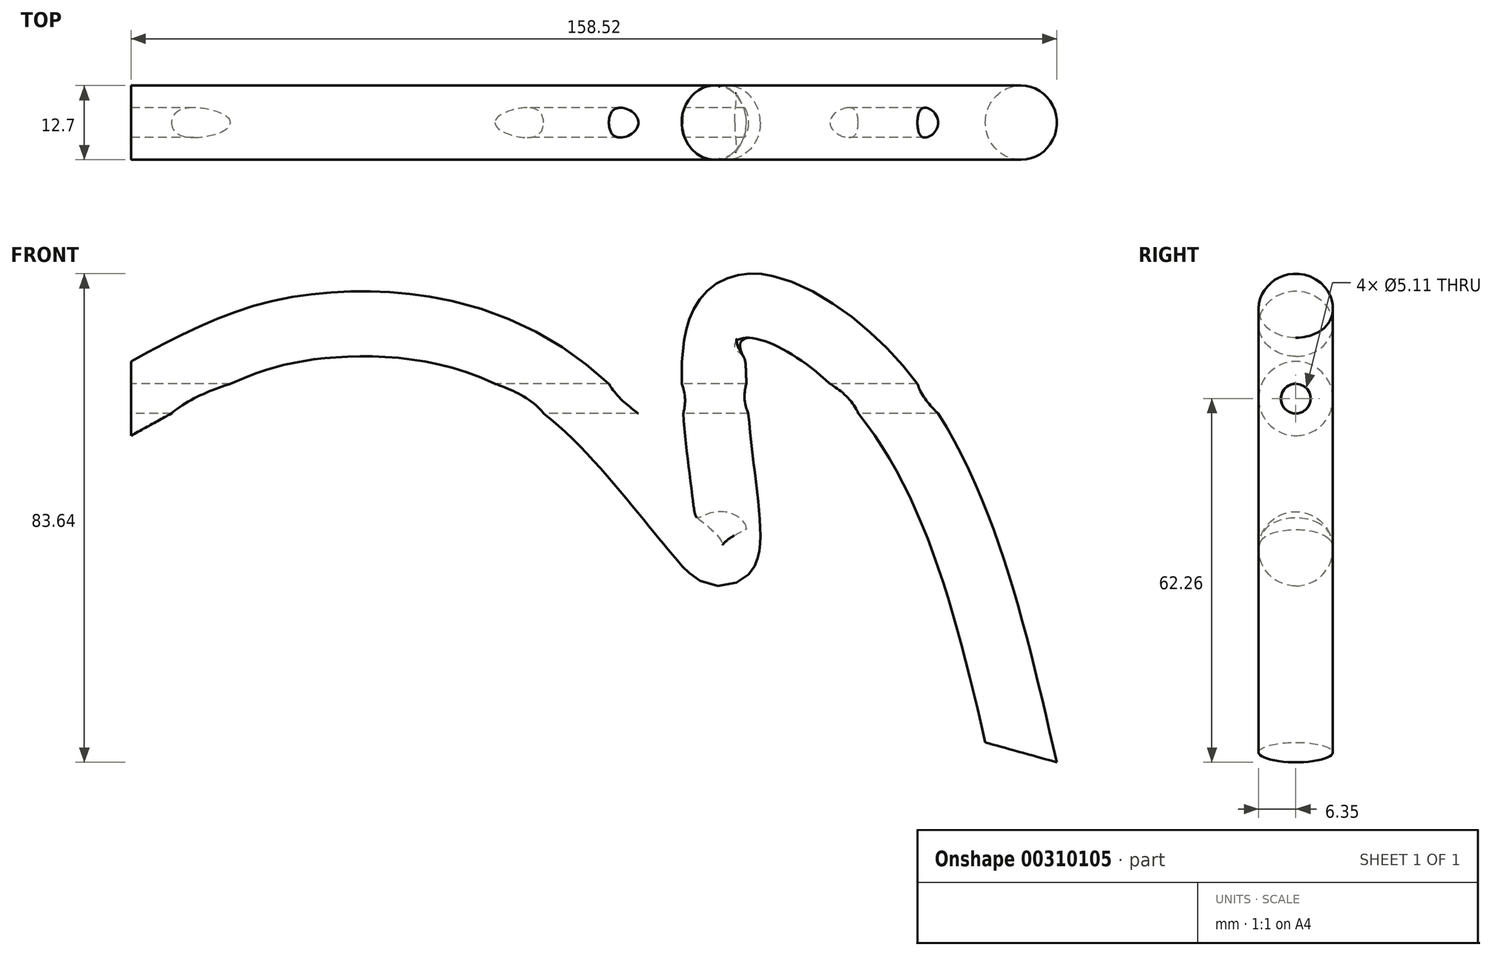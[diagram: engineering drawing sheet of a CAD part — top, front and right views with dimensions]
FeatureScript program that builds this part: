
annotation { "Feature Type Name" : "Feature", "Feature Type Description" : "" }
export const myFeature = defineFeature(function(context is Context, id is Id, definition is map)
    precondition{}
    {
        {
            var Q0;
            Q0=qCreatedBy(makeId("Right.planeOp"),FACE);
            cPlane(context, id + "F0", {"entities" : qUnion([Q0]), "cplaneType" : CPlaneType.OFFSET, "offset" : 76.2 * mm, "oppositeDirection" : true, "width" : 152.4 * mm, "height" : 152.4 * mm});
        }
        {
            var Q0;
            Q0=qCreatedBy(makeId("Front.planeOp"),FACE);
            var sketch = newSketch(context, id + "F1", { "sketchPlane" : qUnion([Q0])});
            skLineSegment(sketch, "E0", {"start": v(0, 0) * mm, "end": v(-76.2, 0) * mm, "construction": true});
            skLineSegment(sketch, "E1", {"start": v(-38.1, 0) * mm, "end": v(-38.1, 12.7) * mm, "construction": true});
            skLineSegment(sketch, "E2", {"start": v(25.4, 12.7) * mm, "end": v(25.4, -25.4) * mm, "construction": true});
            skLineSegment(sketch, "E3", {"start": v(-38.1, 12.7) * mm, "end": v(25.4, 12.7) * mm, "construction": true});
            skLineSegment(sketch, "E4", {"start": v(25.4, -25.4) * mm, "end": v(50.8, -25.4) * mm, "construction": true});
            skLineSegment(sketch, "E5", {"start": v(50.8, -25.4) * mm, "end": v(50.8, 2.95) * mm, "construction": true});
            skLineSegment(sketch, "E6", {"start": v(76.2, 2.95) * mm, "end": v(76.2, -60.55) * mm, "construction": true});
            skLineSegment(sketch, "E7", {"start": v(50.8, 2.95) * mm, "end": v(76.2, 2.95) * mm, "construction": true});
            skFitSpline(sketch, "E8", {"points": [v(-76.2, 0) * mm, v(-57.91, 9) * mm, v(-38.1, 12.7) * mm, v(0, 0) * mm, v(25.4, -25.4) * mm, v(25.4, 12.7) * mm, v(50.8, 2.95) * mm, v(76.2, -60.55) * mm], "startDerivative": vector(166.23, 91.12) * mm, "endDerivative": vector(83.05, -355.64) * mm});
            skSolve(sketch);
        }
        {
            var Q0;
            Q0=qCreatedBy(id+"F0.planeOp",FACE);
            var sketch = newSketch(context, id + "F2", { "sketchPlane" : qUnion([Q0])});
            skCircle(sketch, "E9", {"center": v(0, 0) * mm, "radius": 6.35 * mm});
            skSolve(sketch);
        }
        {
            var Q0;
            Q0=makeQuery(id+"F2.imprint","IMPRINT",FACE,{"disambiguationData":[TD([[makeQuery(id+"F2.imprint","IMPRINT",EDGE,{"derivedFrom":sQuery(id+"F2.wireOp",EDGE,"E9")}),1.0]])]});
            var Q1;
            Q1=sQuery(id+"F1.wireOp",EDGE,"E8");
            sweep(context, id + "F3", {"profiles" : qUnion([Q0]), "path" : qUnion([Q1])});
        }
        {
            var Q0;
            Q0=sQuery(id+"F2.wireOp",VERTEX,"E9.center");
            var Q1;
            Q1=makeQuery(id+"F3.opSweep","SWEPT_BODY",BODY,{"disambiguationData":[OSD([sQuery(id+"F1.wireOp",EDGE,"E8"),sQuery(id+"F2.wireOp",EDGE,"E9")])]});
            hole(context, id + "F4", {"style" : HoleStyle.SIMPLE, "endStyle" : HoleEndStyle.THROUGH, "oppositeDirection" : true, "standardTappedOrClearance" : lookupTablePath({ "standard" : "ANSI", "engagement" : "75%", "pitch" : "20 tpi", "size" : "1/4", "type" : "Tapped" }), "standardBlindInLast" : lookupTablePath({ "standard" : "ANSI", "engagement" : "75%", "pitch" : "20 tpi", "size" : "1/4", "type" : "Tapped" }), "holeDiameter" : 5.1 * mm, "showTappedDepth" : true, "tappedDepth" : 25.4 * mm, "tapClearance" : 3, "locations" : qUnion([Q0]), "scope" : qUnion([Q1]), "majorDiameter" : 6.35 * mm});
        }
    });
